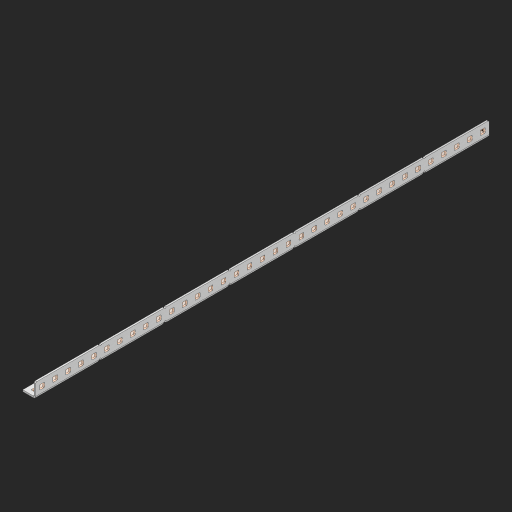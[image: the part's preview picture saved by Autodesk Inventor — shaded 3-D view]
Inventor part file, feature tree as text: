
AUTODESK INVENTOR PART (.ipt)
format: ipt  version: 2023 (Build 270158000, 158)  size: 1,056,256 bytes
history: native  units: in
note: dims shown in document units (in); Inventor stores cm internally (conversion verified against a paired STEP export)
features: other x75, extrude x69, sheet_metal_op x10, sketch x8, mirror x1, pattern_linear x1, chamfer x1
ambient origin geometry x8: Origin, YZ Plane, XZ Plane, XY Plane, X Axis, Y Axis, Z Axis, Center Point
bodies: Solid1 (feature_tree), Body (feature_tree)
feature tree (165):
  other  "Flange Pattern Plane"
  sheet_metal_op  "Flange Pattern"
  sheet_metal_op  "Body Pattern"
  other  "Arc Length"
  mirror  "Notch Mirror"
  pattern_linear  "Notch Pattern"  Spacing1=0.25in  [1 undecoded]
  chamfer  "End Chamfer"
  extrude  "Half Cut"  Depth=0.0625in
  sketch  "Sketch1"  dims[d0=1.5in]
  other  "Plate1"
  sketch  "Sketch2"  dims[d1=17.5in]
  other  "Plate2"
  sheet_metal_op  "Bend1"
  sheet_metal_op  "Corner1"
  sketch  "Sketch3"  dims[d2=0.0625in]
  other  "Flange Pattern Sketch"
  sketch  "Sketch7"  dims[d3=0.0625in]
  other  "Srf1"
  other  "Srf2"
  sketch  "Sketch8"  dims[d4=0.0312in]
  sketch  "Sketch9"  dims[d5=0.125in]
  other  "Srf91"
  sheet_metal_op  "Body Pattern Sketch"
  other  "Srf92"
  sketch  "Sketch13"  dims[d6=0.0625in]
  sketch  "Sketch14"  dims[d7=0.5in d8=90.0deg d9=0.0312in d10=0.25in d11=0.0625in d12=0.0625in d16=0.182in d17=0.02in d18=0.0625in d19=0.0in d20=0.25in d21=0.25in d46=0.172in d47=1.0in d48=0.0in d49=0.182in d50=0.02in d51=0.25in d52=0.25in d53=0.0625in d54=0.0in d55=0.172in d56=1.0in d57=0.0in d60=13.7795in d62=0.5in d63=0.3937in d65=0.5in d85=0.1473in d86=0.1782in d88=0.04in d89=0.0625in d90=0.0in d91=0.04in d92=0.0491in d95=2.5in d96=0.04in d97=0.25in d98=45.0deg d101=0.0in d102=2.497in d131=0.5in d132=13.7795in d134=0.5in d139=0.5in]
  other  "Srf856"
  other  "Srf1310"
  other  "Srf1311"
  other  "Srf1312"
  other  "Srf1376"
  other  "Srf1377"
  other  "Srf1728"
  other  "Srf1755"
  other  "Srf1878"
  other  "Srf1879"
  other  "Srf1880"
  other  "Srf1881"
  other  "Srf1882"
  other  "Srf1883"
  other  "Srf1884"
  other  "Srf1885"
  other  "Srf1886"
  other  "Srf1887"
  other  "Srf1888"
  other  "Srf1889"
  other  "Srf1890"
  other  "Srf1891"
  other  "Srf1892"
  other  "Srf1893"
  other  "Srf1894"
  other  "Srf1895"
  other  "Srf1896"
  other  "Srf1897"
  other  "Srf1898"
  other  "Srf1899"
  other  "Srf1900"
  other  "Srf1901"
  other  "Srf1902"
  other  "Srf1903"
  other  "Srf1904"
  other  "Srf1905"
  other  "Srf1906"
  other  "Srf1942"
  other  "Srf1943"
  other  "Srf1944"
  other  "Srf1945"
  other  "Srf1946"
  other  "Srf1947"
  other  "Srf1948"
  other  "Srf1949"
  other  "Srf1950"
  other  "Srf1951"
  other  "Srf1952"
  other  "Srf1953"
  other  "Srf1954"
  other  "Srf1955"
  other  "Srf1956"
  other  "Srf1957"
  other  "Srf1958"
  other  "Srf1959"
  other  "Srf1960"
  other  "Srf1961"
  other  "Srf1962"
  other  "Srf1963"
  other  "Srf1964"
  other  "Srf1965"
  other  "Srf1966"
  other  "Srf1967"
  other  "Srf1968"
  other  "Srf1969"
  other  "Srf1970"
  sheet_metal_op  "Flange Stamp"
  sheet_metal_op  "Flange Circle"
  sheet_metal_op  "Body Stamp"
  sheet_metal_op  "Body Circle"
  sheet_metal_op  "Notch"
  extrude  "ExtrusionSrf2"  Depth=0.0625in
  extrude  "ExtrusionSrf92"  Depth=0.5in
  extrude  "ExtrusionSrf856"  Depth=0.02in
  extrude  "ExtrusionSrf1310"  Depth=0.0625in
  extrude  "ExtrusionSrf1311"  TaperAngle=0.0deg  [1 undecoded]
  extrude  "ExtrusionSrf1312"  Depth=0.5in
  extrude  "ExtrusionSrf1376"  Depth=0.5in
  extrude  "ExtrusionSrf1377"  Depth=0.5in
  extrude  "ExtrusionSrf1728"  Depth=0.5in TaperAngle=0.0deg
  extrude  "ExtrusionSrf1755"  Depth=0.5in
  extrude  "ExtrusionSrf1878"  Depth=0.02in
  extrude  "ExtrusionSrf1879"  Depth=0.5in
  extrude  "ExtrusionSrf1880"  Depth=0.5in
  extrude  "ExtrusionSrf1881"  Depth=0.0625in
  extrude  "ExtrusionSrf1882"  TaperAngle=0.0deg  [1 undecoded]
  extrude  "ExtrusionSrf1883"  Depth=0.5in
  extrude  "ExtrusionSrf1884"  Depth=0.5in TaperAngle=0.0deg
  extrude  "ExtrusionSrf1885"  Depth=0.5in
  extrude  "ExtrusionSrf1886"  Depth=0.5in
  extrude  "ExtrusionSrf1887"  Depth=0.5in
  extrude  "ExtrusionSrf1888"  Depth=0.5in
  extrude  "ExtrusionSrf1889"  Depth=0.5in
  extrude  "ExtrusionSrf1890"  Depth=0.0625in
  extrude  "ExtrusionSrf1891"  TaperAngle=0.0deg  [1 undecoded]
  extrude  "ExtrusionSrf1892"  Depth=0.5in
  extrude  "ExtrusionSrf1893"  Depth=0.5in
  extrude  "ExtrusionSrf1894"  Depth=0.5in
  extrude  "ExtrusionSrf1895"  Depth=0.5in TaperAngle=45.0deg
  extrude  "ExtrusionSrf1896"  TaperAngle=0.0deg  [1 undecoded]
  extrude  "ExtrusionSrf1897"  Depth=0.5in
  extrude  "ExtrusionSrf1898"  Depth=0.5in
  extrude  "ExtrusionSrf1899"  Depth=0.5in
  extrude  "ExtrusionSrf1900"  Depth=0.5in
  extrude  "ExtrusionSrf1901"  Depth=0.5in
  extrude  "ExtrusionSrf1902"  [1 undecoded]
  extrude  "ExtrusionSrf1903"  [1 undecoded]
  extrude  "ExtrusionSrf1904"  [1 undecoded]
  extrude  "ExtrusionSrf1905"  [1 undecoded]
  extrude  "ExtrusionSrf1906"  [1 undecoded]
  extrude  "ExtrusionSrf1942"  [1 undecoded]
  extrude  "ExtrusionSrf1943"  [1 undecoded]
  extrude  "ExtrusionSrf1944"  [1 undecoded]
  extrude  "ExtrusionSrf1945"  [1 undecoded]
  extrude  "ExtrusionSrf1946"  [1 undecoded]
  extrude  "ExtrusionSrf1947"  [1 undecoded]
  extrude  "ExtrusionSrf1948"  [1 undecoded]
  extrude  "ExtrusionSrf1949"  [1 undecoded]
  extrude  "ExtrusionSrf1950"  [1 undecoded]
  extrude  "ExtrusionSrf1951"  [1 undecoded]
  extrude  "ExtrusionSrf1952"  [1 undecoded]
  extrude  "ExtrusionSrf1953"  [1 undecoded]
  extrude  "ExtrusionSrf1954"  [1 undecoded]
  extrude  "ExtrusionSrf1955"  [1 undecoded]
  extrude  "ExtrusionSrf1956"  [1 undecoded]
  extrude  "ExtrusionSrf1957"  [1 undecoded]
  extrude  "ExtrusionSrf1958"  [1 undecoded]
  extrude  "ExtrusionSrf1959"  [1 undecoded]
  extrude  "ExtrusionSrf1960"  [1 undecoded]
  extrude  "ExtrusionSrf1961"  [1 undecoded]
  extrude  "ExtrusionSrf1962"  [1 undecoded]
  extrude  "ExtrusionSrf1963"  [1 undecoded]
  extrude  "ExtrusionSrf1964"  [1 undecoded]
  extrude  "ExtrusionSrf1965"  [1 undecoded]
  extrude  "ExtrusionSrf1966"  [1 undecoded]
  extrude  "ExtrusionSrf1967"  [1 undecoded]
  extrude  "ExtrusionSrf1968"  [1 undecoded]
  extrude  "ExtrusionSrf1969"  [1 undecoded]
  extrude  "ExtrusionSrf1970"  [1 undecoded]
note: 39 required parameter values undecoded (feature->parameter linkage not recoverable at this tier; creation-order binding heuristic only, values carry confidence <= 0.55)
